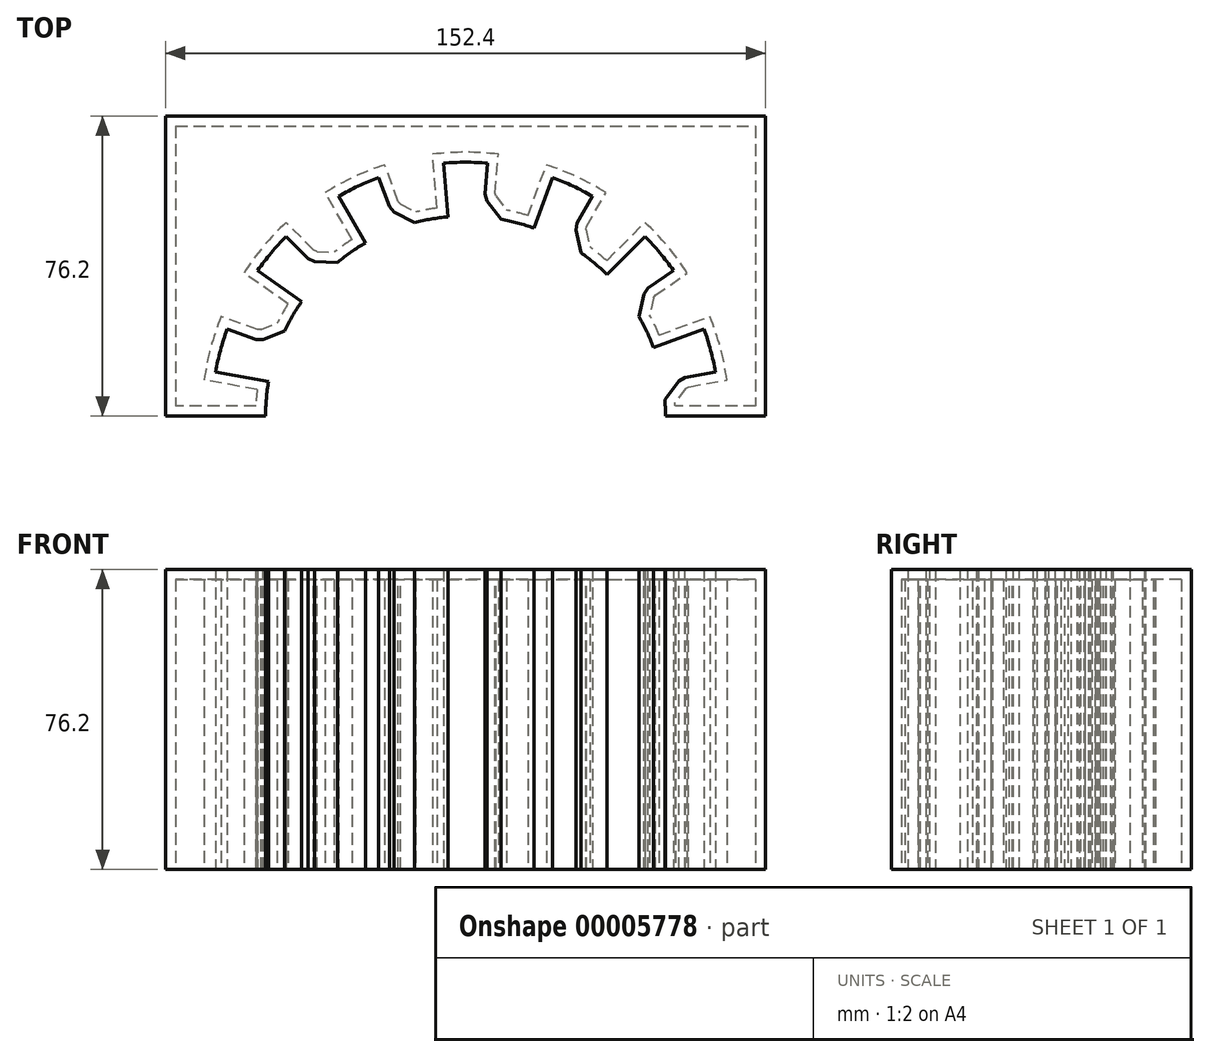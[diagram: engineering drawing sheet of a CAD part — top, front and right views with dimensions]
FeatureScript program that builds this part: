
annotation { "Feature Type Name" : "Feature", "Feature Type Description" : "" }
export const myFeature = defineFeature(function(context is Context, id is Id, definition is map)
    precondition{}
    {
        {
            var Q0;
            Q0=qCreatedBy(makeId("Top.planeOp"),FACE);
            var sketch = newSketch(context, id + "F0", { "sketchPlane" : qUnion([Q0])});
            skLineSegment(sketch, "E0.bottom", {"start": v(-76.2, 76.2) * mm, "end": v(76.2, 76.2) * mm});
            skLineSegment(sketch, "E0.left", {"start": v(-76.2, 76.2) * mm, "end": v(-76.2, 0) * mm});
            skLineSegment(sketch, "E0.right", {"start": v(76.2, 76.2) * mm, "end": v(76.2, 0) * mm});
            skPoint(sketch, "E1", {"position": v(0, 76.2) * mm});
            skArc(sketch, "E2", {"start": v(50.8, 0) * mm, "mid": v(0, 50.8) * mm, "end": v(-50.8, 0) * mm});
            skLineSegment(sketch, "E3", {"start": v(76.2, 0) * mm, "end": v(50.8, 0) * mm});
            skLineSegment(sketch, "E4", {"start": v(-50.8, 0) * mm, "end": v(-76.2, 0) * mm});
            skSolve(sketch);
        }
        {
            var Q0;
            Q0=makeQuery(id+"F0.imprint","IMPRINT",FACE,{"disambiguationData":[TD([[makeQuery(id+"F0.imprint","IMPRINT",EDGE,{"derivedFrom":sQuery(id+"F0.wireOp",EDGE,"E0.bottom")}),-1.0]])]});
            extrude(context, id + "F1", {"entities" : qUnion([Q0]), "depth" : 76.2 * mm});
        }
        {
            var Q0;
            Q0=qCreatedBy(makeId("Top.planeOp"),FACE);
            var sketch = newSketch(context, id + "F2", { "sketchPlane" : qUnion([Q0])});
            skLineSegment(sketch, "E5", {"start": v(0, 0) * mm, "end": v(-63.5, 11.2) * mm, "construction": true});
            skLineSegment(sketch, "E6", {"start": v(0, 0) * mm, "end": v(-60.6, 22.05) * mm, "construction": true});
            skArc(sketch, "E7", {"start": v(-60.6, 22.05) * mm, "mid": v(-62.28, 16.69) * mm, "end": v(-63.5, 11.2) * mm});
            skArc(sketch, "E8.0", {"start": v(-47.74, 17.37) * mm, "mid": v(-50.03, 8.82) * mm, "end": v(-50.8, 0) * mm});
            skPoint(sketch, "E9.orphan", {"position": v(50.8, 0) * mm});
            skLineSegment(sketch, "E10", {"start": v(-47.74, 17.37) * mm, "end": v(-60.6, 22.05) * mm});
            skLineSegment(sketch, "E11", {"start": v(-50.03, 8.82) * mm, "end": v(-63.5, 11.2) * mm});
            skLineSegment(sketch, "E12", {"start": v(0, 0) * mm, "end": v(-50.8, 0) * mm, "construction": true});
            skSolve(sketch);
        }
        {
            var Q0;
            Q0=makeQuery(id+"F2.imprint","IMPRINT",FACE,{"disambiguationData":[TD([[makeQuery(id+"F2.imprint","IMPRINT",EDGE,{"derivedFrom":sQuery(id+"F2.wireOp",EDGE,"E7")}),1.0]])]});
            extrude(context, id + "F3", {"entities" : qUnion([Q0]), "operationType" : NewBodyOperationType.REMOVE, "endBound" : BoundingType.UP_TO_NEXT, "depth" : 25.4 * mm});
        }
        {
            var Q0;
            Q0=makeQuery(id+"F3.boolean.opBoolean","COPY",EDGE,{"derivedFrom":makeQuery(id+"F3.opExtrude","SWEPT_EDGE",EDGE,{"disambiguationData":[OSD([sQuery(id+"F2.wireOp",EDGE,"E8.0"),sQuery(id+"F2.wireOp",EDGE,"E10")])]})});
            var Q1;
            Q1=makeQuery(id+"F3.boolean.opBoolean","COPY",EDGE,{"derivedFrom":makeQuery(id+"F3.opExtrude","SWEPT_EDGE",EDGE,{"disambiguationData":[OSD([sQuery(id+"F2.wireOp",EDGE,"E8.0"),sQuery(id+"F2.wireOp",EDGE,"E11")])]})});
            chamfer(context, id + "F4", {"entities" : qUnion([Q0, Q1]), "width" : 5.08 * mm, "tangentPropagation" : true});
        }
        {
            var Q0;
            {var subQ0=sQuery(id+"F2.wireOp",EDGE,"E10");Q0=makeQuery(id+"F4.opChamfer","BLEND_EDGE",EDGE,{"blendedFrom":[makeQuery(id+"F3.boolean.opBoolean","COPY",EDGE,{"derivedFrom":makeQuery(id+"F3.opExtrude","SWEPT_EDGE",EDGE,{"disambiguationData":[OSD([sQuery(id+"F2.wireOp",EDGE,"E8.0"),subQ0])]})}),makeQuery(id+"F3.boolean.opBoolean","COPY",FACE,{"derivedFrom":makeQuery(id+"F3.opExtrude","SWEPT_FACE",FACE,{"disambiguationData":[OSD([subQ0])]})})],"blendedInto":[makeQuery(id+"F3.boolean.opBoolean","COPY",FACE,{"derivedFrom":makeQuery(id+"F3.opExtrude","SWEPT_FACE",FACE,{"disambiguationData":[OSD([subQ0])]})})]});}
            var Q1;
            {var subQ0=sQuery(id+"F2.wireOp",EDGE,"E11");Q1=makeQuery(id+"F4.opChamfer","BLEND_EDGE",EDGE,{"blendedFrom":[makeQuery(id+"F3.boolean.opBoolean","COPY",EDGE,{"derivedFrom":makeQuery(id+"F3.opExtrude","SWEPT_EDGE",EDGE,{"disambiguationData":[OSD([sQuery(id+"F2.wireOp",EDGE,"E8.0"),subQ0])]})}),makeQuery(id+"F3.boolean.opBoolean","COPY",FACE,{"derivedFrom":makeQuery(id+"F3.opExtrude","SWEPT_FACE",FACE,{"disambiguationData":[OSD([subQ0])]})})],"blendedInto":[makeQuery(id+"F3.boolean.opBoolean","COPY",FACE,{"derivedFrom":makeQuery(id+"F3.opExtrude","SWEPT_FACE",FACE,{"disambiguationData":[OSD([subQ0])]})})]});}
            chamfer(context, id + "F5", {"entities" : qUnion([Q0, Q1]), "width" : 2.54 * mm, "tangentPropagation" : true});
        }
        {
            var Q0;
            Q0=qCreatedBy(makeId("Front.planeOp"),FACE);
            var sketch = newSketch(context, id + "F6", { "sketchPlane" : qUnion([Q0])});
            skLineSegment(sketch, "E13", {"start": v(0, 0) * mm, "end": v(0, 127) * mm, "construction": true});
            skSolve(sketch);
        }
        {
            var Q0;
            Q0=makeQuery(id+"F5.opChamfer","BLEND_FACE",FACE,{"disambiguationData":[OSD([sQuery(id+"F2.wireOp",EDGE,"E8.0"),sQuery(id+"F2.wireOp",EDGE,"E10")])]});
            var Q1;
            Q1=makeQuery(id+"F4.opChamfer","BLEND_FACE",FACE,{"disambiguationData":[OSD([sQuery(id+"F2.wireOp",EDGE,"E8.0"),sQuery(id+"F2.wireOp",EDGE,"E10")])]});
            var Q2;
            Q2=makeQuery(id+"F3.boolean.opBoolean","COPY",FACE,{"derivedFrom":makeQuery(id+"F3.opExtrude","SWEPT_FACE",FACE,{"disambiguationData":[OSD([sQuery(id+"F2.wireOp",EDGE,"E10")])]})});
            var Q3;
            Q3=makeQuery(id+"F3.boolean.opBoolean","COPY",FACE,{"derivedFrom":makeQuery(id+"F3.opExtrude","SWEPT_FACE",FACE,{"disambiguationData":[OSD([sQuery(id+"F2.wireOp",EDGE,"E7")])]})});
            var Q4;
            Q4=makeQuery(id+"F3.boolean.opBoolean","COPY",FACE,{"derivedFrom":makeQuery(id+"F3.opExtrude","SWEPT_FACE",FACE,{"disambiguationData":[OSD([sQuery(id+"F2.wireOp",EDGE,"E11")])]})});
            var Q5;
            Q5=makeQuery(id+"F5.opChamfer","BLEND_FACE",FACE,{"disambiguationData":[OSD([sQuery(id+"F2.wireOp",EDGE,"E8.0"),sQuery(id+"F2.wireOp",EDGE,"E11")])]});
            var Q6;
            Q6=makeQuery(id+"F4.opChamfer","BLEND_FACE",FACE,{"disambiguationData":[OSD([sQuery(id+"F2.wireOp",EDGE,"E8.0"),sQuery(id+"F2.wireOp",EDGE,"E11")])]});
            var Q7;
            Q7=sQuery(id+"F6.wireOp",EDGE,"E13");
            circularPattern(context, id + "F7", {"faces" : qUnion([Q0, Q1, Q2, Q3, Q4, Q5, Q6]), "axis" : qUnion([Q7]), "angle" : 25 * degree, "instanceCount" : 7, "oppositeDirection" : true, "patternType" : PatternType.FACE});
        }
        {
            var Q0;
            Q0=makeQuery(id+"F1.opExtrude","CAP_FACE",FACE,{"disambiguationData":[OSD([sQuery(id+"F0.wireOp",EDGE,"E0.bottom"),sQuery(id+"F0.wireOp",EDGE,"E0.left"),sQuery(id+"F0.wireOp",EDGE,"E0.right"),sQuery(id+"F0.wireOp",EDGE,"E2"),sQuery(id+"F0.wireOp",EDGE,"E3"),sQuery(id+"F0.wireOp",EDGE,"E4")])],"isStart":true});
            shell(context, id + "F8", {"entities" : qUnion([Q0]), "thickness" : 2.54 * mm});
        }
    });
